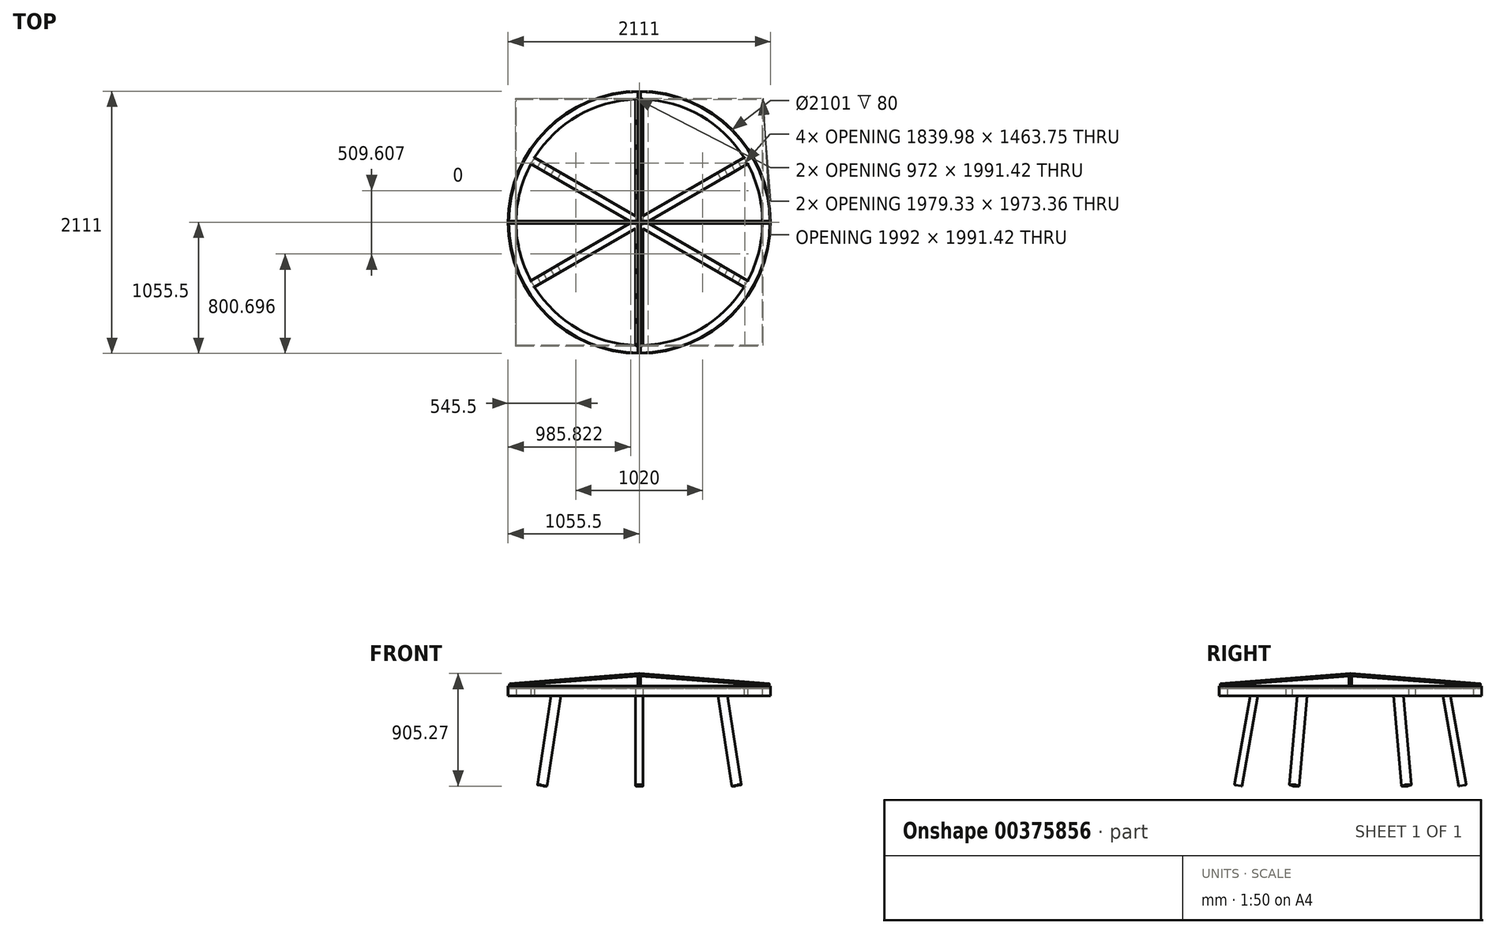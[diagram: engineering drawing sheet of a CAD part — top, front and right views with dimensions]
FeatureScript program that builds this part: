
annotation { "Feature Type Name" : "Feature", "Feature Type Description" : "" }
export const myFeature = defineFeature(function(context is Context, id is Id, definition is map)
    precondition{}
    {
        {
            var Q0;
            Q0=qCreatedBy(makeId("Front.planeOp"),FACE);
            var sketch = newSketch(context, id + "F0", { "sketchPlane" : qUnion([Q0])});
            skLineSegment(sketch, "E0", {"start": v(0, 250) * mm, "end": v(0, -250) * mm, "construction": true});
            skSolve(sketch);
        }
        {
            var Q0;
            Q0=qCreatedBy(makeId("Front.planeOp"),FACE);
            var sketch = newSketch(context, id + "F1", { "sketchPlane" : qUnion([Q0])});
            skLineSegment(sketch, "E1.bottom", {"start": v(-996, 30) * mm, "end": v(-1044, 30) * mm});
            skLineSegment(sketch, "E1.top", {"start": v(-996, -30) * mm, "end": v(-1044, -30) * mm});
            skLineSegment(sketch, "E1.left", {"start": v(-990, 24) * mm, "end": v(-990, -24) * mm});
            skLineSegment(sketch, "E1.right", {"start": v(-1050, 24) * mm, "end": v(-1050, -24) * mm});
            skPoint(sketch, "E1.middle", {"position": v(-1020, 0) * mm});
            skPoint(sketch, "E2.visualSharp", {"position": v(-1050, 30) * mm});
            skArc(sketch, "E2.filletArc", {"start": v(-1044, 30) * mm, "mid": v(-1048.24, 28.24) * mm, "end": v(-1050, 24) * mm});
            skPoint(sketch, "E3.visualSharp", {"position": v(-990, 30) * mm});
            skArc(sketch, "E3.filletArc", {"start": v(-990, 24) * mm, "mid": v(-991.76, 28.24) * mm, "end": v(-996, 30) * mm});
            skPoint(sketch, "E4.visualSharp", {"position": v(-990, -30) * mm});
            skArc(sketch, "E4.filletArc", {"start": v(-996, -30) * mm, "mid": v(-991.76, -28.24) * mm, "end": v(-990, -24) * mm});
            skPoint(sketch, "E5.visualSharp", {"position": v(-1050, -30) * mm});
            skArc(sketch, "E5.filletArc", {"start": v(-1050, -24) * mm, "mid": v(-1048.24, -28.24) * mm, "end": v(-1044, -30) * mm});
            skSolve(sketch);
        }
        {
            var Q0;
            Q0=qCreatedBy(makeId("Top.planeOp"),FACE);
            var sketch = newSketch(context, id + "F2", { "sketchPlane" : qUnion([Q0])});
            skCircle(sketch, "E6", {"center": v(0, 0) * mm, "radius": 1020 * mm, "construction": true});
            skSolve(sketch);
        }
        {
            var Q0;
            Q0=makeQuery(id+"F1.imprint","IMPRINT",FACE,{"disambiguationData":[TD([[makeQuery(id+"F1.imprint","IMPRINT",EDGE,{"derivedFrom":sQuery(id+"F1.wireOp",EDGE,"E1.bottom")}),1.0]])]});
            var Q1;
            Q1=sQuery(id+"F2.wireOp",EDGE,"E6");
            revolve(context, id + "F3", {"entities" : qUnion([Q0]), "axis" : qUnion([Q1]), "revolveType" : RevolveType.FULL});
        }
        {
            var Q0;
            Q0=qCreatedBy(makeId("Front.planeOp"),FACE);
            var sketch = newSketch(context, id + "F4", { "sketchPlane" : qUnion([Q0])});
            skLineSegment(sketch, "E7.bottom", {"start": v(24, 30) * mm, "end": v(-24, 30) * mm});
            skLineSegment(sketch, "E7.top", {"start": v(24, -30) * mm, "end": v(-24, -30) * mm});
            skLineSegment(sketch, "E7.left", {"start": v(30, 24) * mm, "end": v(30, -24) * mm});
            skLineSegment(sketch, "E7.right", {"start": v(-30, 24) * mm, "end": v(-30, -24) * mm});
            skPoint(sketch, "E7.middle", {"position": v(0, 0) * mm});
            skPoint(sketch, "E8.visualSharp", {"position": v(-30, 30) * mm});
            skArc(sketch, "E8.filletArc", {"start": v(-24, 30) * mm, "mid": v(-28.24, 28.24) * mm, "end": v(-30, 24) * mm});
            skPoint(sketch, "E9.visualSharp", {"position": v(-30, -30) * mm});
            skArc(sketch, "E9.filletArc", {"start": v(-30, -24) * mm, "mid": v(-28.24, -28.24) * mm, "end": v(-24, -30) * mm});
            skPoint(sketch, "E10.visualSharp", {"position": v(30, 30) * mm});
            skArc(sketch, "E10.filletArc", {"start": v(30, 24) * mm, "mid": v(28.24, 28.24) * mm, "end": v(24, 30) * mm});
            skPoint(sketch, "E11.visualSharp", {"position": v(30, -30) * mm});
            skArc(sketch, "E11.filletArc", {"start": v(24, -30) * mm, "mid": v(28.24, -28.24) * mm, "end": v(30, -24) * mm});
            skSolve(sketch);
        }
        {
            var Q0;
            Q0 = qSketchRegion(id + "F4", true);
            extrude(context, id + "F5", {"entities" : qUnion([Q0]), "operationType" : NewBodyOperationType.ADD, "depth" : 1030 * mm, "hasSecondDirection" : true, "secondDirectionOppositeDirection" : true, "secondDirectionDepth" : 1030 * mm});
        }
        {
            var Q0;
            Q0=qCreatedBy(makeId("Right.planeOp"),FACE);
            var sketch = newSketch(context, id + "F6", { "sketchPlane" : qUnion([Q0])});
            skLineSegment(sketch, "E12", {"start": v(0, 0) * mm, "end": v(-800, 0) * mm});
            skLineSegment(sketch, "E13", {"start": v(-762.86, 37.85) * mm, "end": v(-901.78, -750) * mm, "construction": true});
            skLineSegment(sketch, "E14", {"start": v(-931.33, -744.8) * mm, "end": v(-872.24, -755.2) * mm, "construction": true});
            skLineSegment(sketch, "E15", {"start": v(-931.33, -744.8) * mm, "end": v(-800, 0) * mm});
            skLineSegment(sketch, "E16", {"start": v(-800, 0) * mm, "end": v(-800, 0) * mm});
            skLineSegment(sketch, "E17", {"start": v(-740.91, -10.42) * mm, "end": v(-872.24, -755.2) * mm});
            skLineSegment(sketch, "E18", {"start": v(-931.33, -744.8) * mm, "end": v(-872.24, -755.2) * mm});
            skLineSegment(sketch, "E19", {"start": v(-800, 0) * mm, "end": v(-740.91, -10.42) * mm});
            skSolve(sketch);
        }
        {
            var Q0;
            Q0 = qSketchRegion(id + "F6", true);
            extrude(context, id + "F7", {"entities" : qUnion([Q0]), "endBound" : BoundingType.SYMMETRIC, "depth" : 60 * mm});
        }
        {
            var Q0;
            Q0=makeQuery(id+"F7.opExtrude","CAP_EDGE",EDGE,{"disambiguationData":[OSD([sQuery(id+"F6.wireOp",EDGE,"E15")])],"isStart":true});
            var Q1;
            Q1=makeQuery(id+"F7.opExtrude","CAP_EDGE",EDGE,{"disambiguationData":[OSD([sQuery(id+"F6.wireOp",EDGE,"E15")])],"isStart":false});
            var Q2;
            Q2=makeQuery(id+"F7.opExtrude","CAP_EDGE",EDGE,{"disambiguationData":[OSD([sQuery(id+"F6.wireOp",EDGE,"E17")])],"isStart":false});
            var Q3;
            Q3=makeQuery(id+"F7.opExtrude","CAP_EDGE",EDGE,{"disambiguationData":[OSD([sQuery(id+"F6.wireOp",EDGE,"E17")])],"isStart":true});
            fillet(context, id + "F8", {"entities" : qUnion([Q0, Q1, Q2, Q3]), "radius" : 6 * mm, "tangentPropagation" : true, "allowEdgeOverflow" : false});
        }
        {
            var Q0;
            Q0=makeQuery(id+"F7.opExtrude","SWEPT_BODY",BODY,{"disambiguationData":[OSD([sQuery(id+"F6.wireOp",EDGE,"E15"),sQuery(id+"F6.wireOp",EDGE,"E17"),sQuery(id+"F6.wireOp",EDGE,"E18"),sQuery(id+"F6.wireOp",EDGE,"E19")])]});
            var Q1;
            Q1=qCreatedBy(makeId("Front.planeOp"),FACE);
            mirror(context, id + "F9", {"operationType" : NewBodyOperationType.ADD, "entities" : qUnion([Q0]), "mirrorPlane" : qUnion([Q1])});
        }
        {
            var Q0;
            Q0=makeQuery(id+"F3.opRevolve","SWEPT_BODY",BODY,{"disambiguationData":[OSD([sQuery(id+"F1.wireOp",EDGE,"E1.bottom"),sQuery(id+"F1.wireOp",EDGE,"E1.top"),sQuery(id+"F1.wireOp",EDGE,"E1.left"),sQuery(id+"F1.wireOp",EDGE,"E1.right"),sQuery(id+"F1.wireOp",EDGE,"E2.filletArc"),sQuery(id+"F1.wireOp",EDGE,"E3.filletArc"),sQuery(id+"F1.wireOp",EDGE,"E4.filletArc"),sQuery(id+"F1.wireOp",EDGE,"E5.filletArc")])]});
            var Q1;
            Q1=sQuery(id+"F0.wireOp",EDGE,"E0");
            circularPattern(context, id + "F10", {"entities" : qUnion([Q0]), "axis" : qUnion([Q1]), "angle" : 360 * degree, "instanceCount" : 6, "equalSpace" : true});
        }
        {
            var Q0;
            Q0=qCreatedBy(makeId("Right.planeOp"),FACE);
            var sketch = newSketch(context, id + "F11", { "sketchPlane" : qUnion([Q0])});
            skLineSegment(sketch, "E20", {"start": v(0, 30) * mm, "end": v(0, 130) * mm, "construction": true});
            skLineSegment(sketch, "E21", {"start": v(1045, 30) * mm, "end": v(0, 30) * mm, "construction": true});
            skLineSegment(sketch, "E22", {"start": v(0, 130) * mm, "end": v(0, 150.06) * mm});
            skLineSegment(sketch, "E23", {"start": v(0, 150.06) * mm, "end": v(1045, 70.06) * mm});
            skLineSegment(sketch, "E24", {"start": v(1045, 30) * mm, "end": v(1045, 50) * mm, "construction": true});
            skLineSegment(sketch, "E25", {"start": v(1045, 70.06) * mm, "end": v(1045, 50) * mm});
            skLineSegment(sketch, "E26", {"start": v(0, 130) * mm, "end": v(1045, 50) * mm});
            skSolve(sketch);
        }
        {
            var Q0;
            Q0 = qSketchRegion(id + "F11", true);
            extrude(context, id + "F12", {"entities" : qUnion([Q0]), "endBound" : BoundingType.SYMMETRIC, "depth" : 5 * mm});
        }
        {
            var Q0;
            Q0=qCreatedBy(makeId("Right.planeOp"),FACE);
            var sketch = newSketch(context, id + "F13", { "sketchPlane" : qUnion([Q0])});
            skLineSegment(sketch, "E27", {"start": v(0, 130) * mm, "end": v(0, 135.01) * mm});
            skLineSegment(sketch, "E28", {"start": v(0, 135.01) * mm, "end": v(1046.95, 55.01) * mm});
            skLineSegment(sketch, "E29", {"start": v(1046.95, 55.01) * mm, "end": v(1046.95, 50) * mm});
            skLineSegment(sketch, "E30", {"start": v(1046.95, 50) * mm, "end": v(0, 130) * mm});
            skSolve(sketch);
        }
        {
            var Q0;
            Q0 = qSketchRegion(id + "F13", true);
            extrude(context, id + "F14", {"entities" : qUnion([Q0]), "operationType" : NewBodyOperationType.ADD, "endBound" : BoundingType.SYMMETRIC, "depth" : 20 * mm});
        }
        {
            var Q0;
            Q0=makeQuery(id+"F14.boolean.opBoolean","INTERSECT",EDGE,{"derivedFrom":[makeQuery(id+"F12.opExtrude","CAP_FACE",FACE,{"disambiguationData":[OSD([sQuery(id+"F11.wireOp",EDGE,"eeeJIr7V-BC1O-qWEY-tzEF-kqbGwrvtfvA1"),sQuery(id+"F11.wireOp",EDGE,"E22"),sQuery(id+"F11.wireOp",EDGE,"E23"),sQuery(id+"F11.wireOp",EDGE,"KKi4iojZ-ISga-QCkF-eqK7-H9Hnf4ywT4vw")])],"isStart":false}),makeQuery(id+"F14.opExtrude","SWEPT_FACE",FACE,{"disambiguationData":[OSD([sQuery(id+"F13.wireOp",EDGE,"E28")])]})]});
            var Q1;
            Q1=makeQuery(id+"F14.boolean.opBoolean","INTERSECT",EDGE,{"derivedFrom":[makeQuery(id+"F12.opExtrude","CAP_FACE",FACE,{"disambiguationData":[OSD([sQuery(id+"F11.wireOp",EDGE,"eeeJIr7V-BC1O-qWEY-tzEF-kqbGwrvtfvA1"),sQuery(id+"F11.wireOp",EDGE,"E22"),sQuery(id+"F11.wireOp",EDGE,"E23"),sQuery(id+"F11.wireOp",EDGE,"KKi4iojZ-ISga-QCkF-eqK7-H9Hnf4ywT4vw")])],"isStart":true}),makeQuery(id+"F14.opExtrude","SWEPT_FACE",FACE,{"disambiguationData":[OSD([sQuery(id+"F13.wireOp",EDGE,"E28")])]})]});
            fillet(context, id + "F15", {"entities" : qUnion([Q0, Q1]), "radius" : 2 * mm, "tangentPropagation" : true, "allowEdgeOverflow" : false});
        }
        {
            var Q0;
            Q0=makeQuery(id+"F14.opExtrude","CAP_EDGE",EDGE,{"disambiguationData":[OSD([sQuery(id+"F13.wireOp",EDGE,"E28")])],"isStart":false});
            var Q1;
            Q1=makeQuery(id+"F14.opExtrude","CAP_EDGE",EDGE,{"disambiguationData":[OSD([sQuery(id+"F13.wireOp",EDGE,"E28")])],"isStart":true});
            var Q2;
            Q2=makeQuery(id+"F12.opExtrude","CAP_EDGE",EDGE,{"disambiguationData":[OSD([sQuery(id+"F11.wireOp",EDGE,"E23")])],"isStart":false});
            var Q3;
            Q3=makeQuery(id+"F12.opExtrude","CAP_EDGE",EDGE,{"disambiguationData":[OSD([sQuery(id+"F11.wireOp",EDGE,"E23")])],"isStart":true});
            fillet(context, id + "F16", {"entities" : qUnion([Q0, Q1, Q2, Q3]), "radius" : 2 * mm, "tangentPropagation" : true, "allowEdgeOverflow" : false});
        }
        {
            var Q0;
            Q0=makeQuery(id+"F12.opExtrude","SWEPT_BODY",BODY,{"disambiguationData":[OSD([sQuery(id+"F11.wireOp",EDGE,"eeeJIr7V-BC1O-qWEY-tzEF-kqbGwrvtfvA1"),sQuery(id+"F11.wireOp",EDGE,"E22"),sQuery(id+"F11.wireOp",EDGE,"E23"),sQuery(id+"F11.wireOp",EDGE,"KKi4iojZ-ISga-QCkF-eqK7-H9Hnf4ywT4vw")])]});
            var Q1;
            Q1=sQuery(id+"F0.wireOp",EDGE,"E0");
            circularPattern(context, id + "F17", {"entities" : qUnion([Q0]), "axis" : qUnion([Q1]), "angle" : 360 * degree, "instanceCount" : 4, "equalSpace" : true});
        }
        {
            var Q0;
            Q0=qCreatedBy(makeId("Front.planeOp"),FACE);
            var sketch = newSketch(context, id + "F18", { "sketchPlane" : qUnion([Q0])});
            skLineSegment(sketch, "E31.bottom", {"start": v(-1050.5, -30) * mm, "end": v(-1055.5, -30) * mm});
            skLineSegment(sketch, "E31.top", {"start": v(-1050.5, 50) * mm, "end": v(-1055.5, 50) * mm});
            skLineSegment(sketch, "E31.left", {"start": v(-1050.5, -30) * mm, "end": v(-1050.5, 50) * mm});
            skLineSegment(sketch, "E31.right", {"start": v(-1055.5, -30) * mm, "end": v(-1055.5, 50) * mm});
            skSolve(sketch);
        }
        {
            var Q0;
            Q0=qCreatedBy(makeId("Top.planeOp"),FACE);
            var sketch = newSketch(context, id + "F19", { "sketchPlane" : qUnion([Q0])});
            skCircle(sketch, "E32", {"center": v(0, 0) * mm, "radius": 1050.5 * mm});
            skSolve(sketch);
        }
        {
            var Q0;
            Q0 = qSketchRegion(id + "F18", true);
            var Q1;
            Q1=sQuery(id+"F19.wireOp",EDGE,"E32");
            revolve(context, id + "F20", {"entities" : qUnion([Q0]), "axis" : qUnion([Q1]), "revolveType" : RevolveType.FULL});
        }
    });
